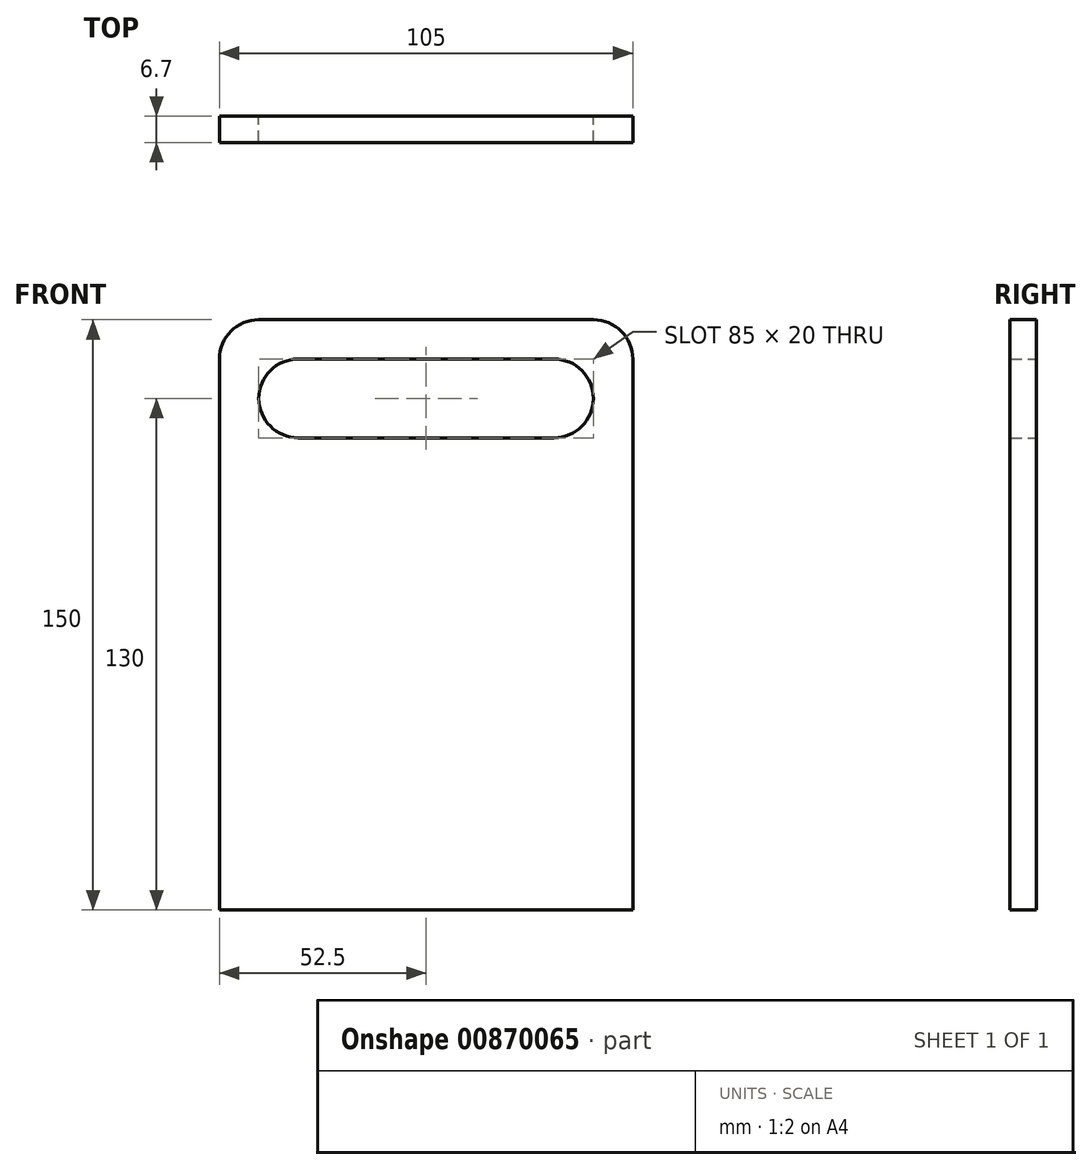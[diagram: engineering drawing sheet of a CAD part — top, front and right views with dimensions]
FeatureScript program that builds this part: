
annotation { "Feature Type Name" : "Feature", "Feature Type Description" : "" }
export const myFeature = defineFeature(function(context is Context, id is Id, definition is map)
    precondition{}
    {
        {
            assignVariable(context, id + "F0", {"name" : "width", "anyValue" : 6.7});
        }
        {
            var Q0;
            Q0=qCreatedBy(makeId("Front.planeOp"),FACE);
            var sketch = newSketch(context, id + "F1", { "sketchPlane" : qUnion([Q0])});
            skLineSegment(sketch, "E0.bottom", {"start": v(42.5, 75) * mm, "end": v(-42.5, 75) * mm});
            skLineSegment(sketch, "E0.top", {"start": v(52.5, -75) * mm, "end": v(-52.5, -75) * mm});
            skLineSegment(sketch, "E0.left", {"start": v(52.5, 65) * mm, "end": v(52.5, -75) * mm});
            skLineSegment(sketch, "E0.right", {"start": v(-52.5, 65) * mm, "end": v(-52.5, -75) * mm});
            skPoint(sketch, "E0.middle", {"position": v(0, 0) * mm});
            skLineSegment(sketch, "E1", {"start": v(-32.5, 55) * mm, "end": v(32.5, 55) * mm, "construction": true});
            skArc(sketch, "E2.0.startCap", {"start": v(-32.5, 45) * mm, "mid": v(-42.5, 55) * mm, "end": v(-32.5, 65) * mm});
            skArc(sketch, "E2.0.endCap", {"start": v(32.5, 65) * mm, "mid": v(42.5, 55) * mm, "end": v(32.5, 45) * mm});
            skLineSegment(sketch, "E2.0.left", {"start": v(-32.5, 65) * mm, "end": v(32.5, 65) * mm});
            skLineSegment(sketch, "E2.0.right", {"start": v(-32.5, 45) * mm, "end": v(32.5, 45) * mm});
            skArc(sketch, "E3.0.startCap", {"start": v(-32.5, 45) * mm, "mid": v(-42.5, 55) * mm, "end": v(-32.5, 65) * mm, "construction": true});
            skArc(sketch, "E3.0.endCap", {"start": v(32.5, 65) * mm, "mid": v(42.5, 55) * mm, "end": v(32.5, 45) * mm, "construction": true});
            skLineSegment(sketch, "E3.0.left", {"start": v(-32.5, 65) * mm, "end": v(32.5, 65) * mm, "construction": true});
            skLineSegment(sketch, "E3.0.right", {"start": v(-32.5, 45) * mm, "end": v(32.5, 45) * mm, "construction": true});
            skPoint(sketch, "E4.visualSharp", {"position": v(-52.5, 75) * mm});
            skArc(sketch, "E4.filletArc", {"start": v(-42.5, 75) * mm, "mid": v(-49.57, 72.07) * mm, "end": v(-52.5, 65) * mm});
            skPoint(sketch, "E5.visualSharp", {"position": v(52.5, 75) * mm});
            skArc(sketch, "E5.filletArc", {"start": v(52.5, 65) * mm, "mid": v(49.57, 72.07) * mm, "end": v(42.5, 75) * mm});
            skSolve(sketch);
        }
        {
            var Q0;
            Q0=makeQuery(id+"F1.imprint","IMPRINT",FACE,{"disambiguationData":[TD([[makeQuery(id+"F1.imprint","IMPRINT",EDGE,{"derivedFrom":sQuery(id+"F1.wireOp",EDGE,"E0.bottom")}),1.0]])]});
            extrude(context, id + "F2", {"entities" : qUnion([Q0]), "depth" : (getVariable(context, 'width')) * mm, "offsetDistance" : 25 * mm});
        }
    });
